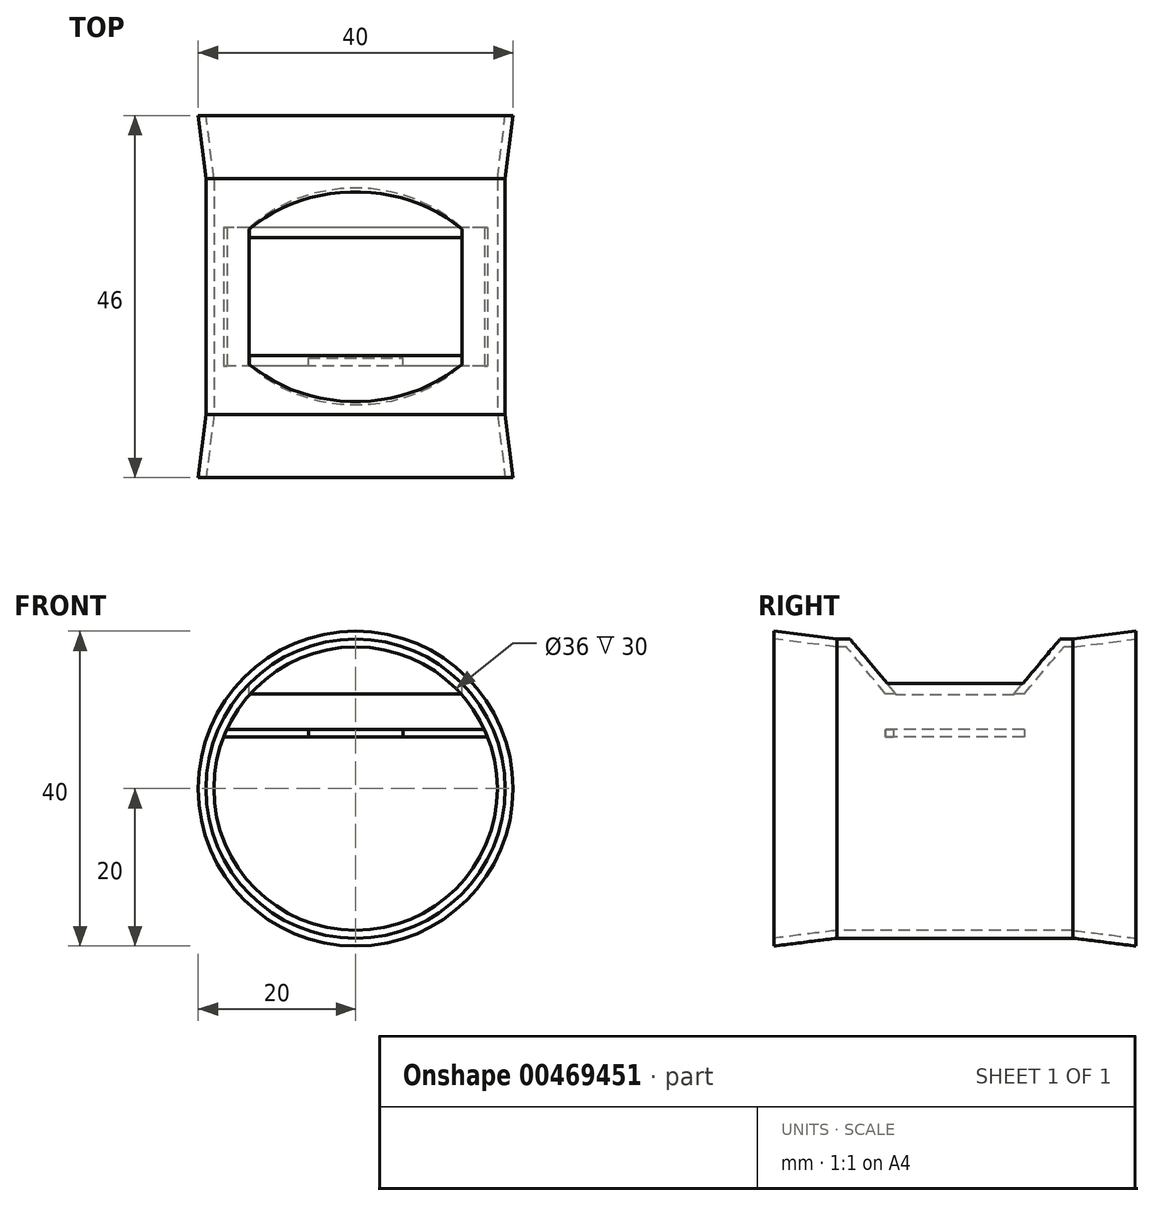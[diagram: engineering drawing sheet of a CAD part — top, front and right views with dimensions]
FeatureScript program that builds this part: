
annotation { "Feature Type Name" : "Feature", "Feature Type Description" : "" }
export const myFeature = defineFeature(function(context is Context, id is Id, definition is map)
    precondition{}
    {
        {
            var Q0;
            Q0=qCreatedBy(makeId("Right.planeOp"),FACE);
            var sketch = newSketch(context, id + "F0", { "sketchPlane" : qUnion([Q0])});
            skLineSegment(sketch, "E0", {"start": v(-23, 19) * mm, "end": v(-15, 18) * mm});
            skLineSegment(sketch, "E1", {"start": v(-15, 18) * mm, "end": v(0, 18) * mm});
            skLineSegment(sketch, "E2.0", {"start": v(-15, 19) * mm, "end": v(0, 19) * mm});
            skLineSegment(sketch, "E3", {"start": v(-15, 19) * mm, "end": v(-23, 20) * mm});
            skLineSegment(sketch, "E4", {"start": v(-23, 20) * mm, "end": v(-23, 19) * mm});
            skLineSegment(sketch, "E5.MirrorCS", {"start": v(23, 20) * mm, "end": v(23, 19) * mm});
            skLineSegment(sketch, "E6.MirrorCS", {"start": v(15, 19) * mm, "end": v(23, 20) * mm});
            skLineSegment(sketch, "E7.MirrorCS", {"start": v(15, 18) * mm, "end": v(0, 18) * mm});
            skLineSegment(sketch, "E8.MirrorCS", {"start": v(23, 19) * mm, "end": v(15, 18) * mm});
            skLineSegment(sketch, "E9.MirrorCS", {"start": v(15, 19) * mm, "end": v(0, 19) * mm});
            skLineSegment(sketch, "E10", {"start": v(-69.17, 0) * mm, "end": v(69.34, 0) * mm});
            skLineSegment(sketch, "E11", {"start": v(-12.5, 18) * mm, "end": v(-7.5, 12.04) * mm});
            skLineSegment(sketch, "E12", {"start": v(-7.5, 12.04) * mm, "end": v(-8.8, 12.04) * mm});
            skLineSegment(sketch, "E13", {"start": v(-8.8, 12.04) * mm, "end": v(-13.8, 18) * mm});
            skLineSegment(sketch, "E14.MirrorCS", {"start": v(12.5, 18) * mm, "end": v(7.5, 12.04) * mm});
            skLineSegment(sketch, "E15.MirrorCS", {"start": v(8.8, 12.04) * mm, "end": v(13.8, 18) * mm});
            skLineSegment(sketch, "E16.MirrorCS", {"start": v(7.5, 12.04) * mm, "end": v(8.8, 12.04) * mm});
            skLineSegment(sketch, "E17", {"start": v(-7.5, 12.04) * mm, "end": v(7.5, 12.04) * mm});
            skLineSegment(sketch, "E18", {"start": v(12.5, 18) * mm, "end": v(13.34, 19) * mm});
            skLineSegment(sketch, "E19", {"start": v(-12.5, 18) * mm, "end": v(-13.34, 19) * mm});
            skLineSegment(sketch, "E20.bottom", {"start": v(-8.8, 7.54) * mm, "end": v(8.8, 7.54) * mm});
            skLineSegment(sketch, "E20.top", {"start": v(-8.8, 6.54) * mm, "end": v(8.8, 6.54) * mm});
            skLineSegment(sketch, "E20.left", {"start": v(-8.8, 7.54) * mm, "end": v(-8.8, 6.54) * mm});
            skLineSegment(sketch, "E20.right", {"start": v(8.8, 7.54) * mm, "end": v(8.8, 6.54) * mm});
            skLineSegment(sketch, "E21", {"start": v(-7.5, 12.04) * mm, "end": v(-7.5, 11.04) * mm});
            skLineSegment(sketch, "E22", {"start": v(-7.5, 11.04) * mm, "end": v(7.5, 11.04) * mm});
            skLineSegment(sketch, "E23", {"start": v(7.5, 11.04) * mm, "end": v(7.5, 12.04) * mm});
            skLineSegment(sketch, "E24", {"start": v(-7.8, 7.54) * mm, "end": v(-7.8, 6.54) * mm});
            skSolve(sketch);
        }
        {
            var Q0;
            {var subQ5=sQuery(id+"F0.wireOp",EDGE,"E0");Q0=makeQuery(id+"F0.imprint","IMPRINT",FACE,{"disambiguationData":[TD([[makeQuery(id+"F0.imprint","IMPRINT",EDGE,{"derivedFrom":subQ5}),1.0]])]});}
            var Q1;
            {var subQ0=sQuery(id+"F0.wireOp",EDGE,"wl3TgNvH-qM2r-iR0o-pi6W-xrNkjA2WT0vf");var subQ1=sQuery(id+"F0.wireOp",EDGE,"E7.MirrorCS");var subQ2=makeQuery(id+"F0.imprint","INTERSECT",VERTEX,{"derivedFrom":[subQ1,subQ0]});Q1=makeQuery(id+"F0.imprint","IMPRINT",FACE,{"disambiguationData":[TD([[makeQuery(id+"F0.imprint","IMPRINT",EDGE,{"disambiguationData":[TD([[subQ2,-1.0]])],"derivedFrom":subQ1}),-1.0]])]});}
            var Q2;
            {var subQ0=sQuery(id+"F0.wireOp",EDGE,"aRFnVEm7-WrF1-xs9J-EZC0-NmZMYpQ3PLDA");var subQ1=sQuery(id+"F0.wireOp",EDGE,"E1");var subQ2=makeQuery(id+"F0.imprint","INTERSECT",VERTEX,{"derivedFrom":[subQ1,subQ0]});Q2=makeQuery(id+"F0.imprint","IMPRINT",FACE,{"disambiguationData":[TD([[makeQuery(id+"F0.imprint","IMPRINT",EDGE,{"disambiguationData":[TD([[subQ2,-1.0]])],"derivedFrom":subQ1}),1.0]])]});}
            var Q3;
            Q3=makeQuery(id+"F0.imprint","IMPRINT",FACE,{"disambiguationData":[TD([[makeQuery(id+"F0.imprint","IMPRINT",EDGE,{"derivedFrom":sQuery(id+"F0.wireOp",EDGE,"E5.MirrorCS")}),-1.0]])]});
            var Q4;
            {var subQ7=sQuery(id+"F0.wireOp",EDGE,"E7.MirrorCS");var subQ9=sQuery(id+"F0.wireOp",EDGE,"E1");var subQ10=makeQuery(id+"F0.imprint","INTERSECT",VERTEX,{"derivedFrom":[subQ9,subQ7]});Q4=makeQuery(id+"F0.imprint","IMPRINT",FACE,{"disambiguationData":[TD([[makeQuery(id+"F0.imprint","IMPRINT",EDGE,{"disambiguationData":[TD([[subQ10,1.0]])],"derivedFrom":subQ9}),1.0]])]});}
            var Q5;
            Q5=sQuery(id+"F0.wireOp",EDGE,"E10");
            revolve(context, id + "F1", {"entities" : qUnion([Q0, Q1, Q2, Q3, Q4]), "axis" : qUnion([Q5]), "revolveType" : RevolveType.FULL});
        }
        {
            var Q0;
            {var subQ0=sQuery(id+"F0.wireOp",EDGE,"E14.MirrorCS");Q0=makeQuery(id+"F0.imprint","IMPRINT",FACE,{"disambiguationData":[TD([[makeQuery(id+"F0.imprint","IMPRINT",EDGE,{"derivedFrom":subQ0}),1.0]])]});}
            var Q1;
            {var subQ0=sQuery(id+"F0.wireOp",EDGE,"E11");Q1=makeQuery(id+"F0.imprint","IMPRINT",FACE,{"disambiguationData":[TD([[makeQuery(id+"F0.imprint","IMPRINT",EDGE,{"derivedFrom":subQ0}),-1.0]])]});}
            var Q2;
            Q2=makeQuery(id+"F1.opRevolve","SWEPT_FACE",FACE,{"disambiguationData":[OSD([sQuery(id+"F0.wireOp",EDGE,"E1"),sQuery(id+"F0.wireOp",EDGE,"E7.MirrorCS")])]});
            var Q3;
            Q3=makeQuery(id+"F1.opRevolve","SWEPT_FACE",FACE,{"disambiguationData":[OSD([sQuery(id+"F0.wireOp",EDGE,"E1"),sQuery(id+"F0.wireOp",EDGE,"E7.MirrorCS")])]});
            extrude(context, id + "F2", {"entities" : qUnion([Q0, Q1]), "operationType" : NewBodyOperationType.ADD, "endBound" : BoundingType.UP_TO_SURFACE, "depth" : 25 * mm, "endBoundEntityFace" : qUnion([Q2]), "offsetDistance" : 25 * mm, "hasSecondDirection" : true, "secondDirectionBound" : SecondDirectionBoundingType.UP_TO_SURFACE, "secondDirectionOppositeDirection" : true, "secondDirectionDepth" : 25 * mm, "secondDirectionBoundEntityFace" : qUnion([Q3])});
        }
        {
            var Q0;
            {var subQ3=sQuery(id+"F0.wireOp",EDGE,"E18");Q0=makeQuery(id+"F0.imprint","IMPRINT",FACE,{"disambiguationData":[TD([[makeQuery(id+"F0.imprint","IMPRINT",EDGE,{"derivedFrom":subQ3}),1.0]])]});}
            var Q1;
            {var subQ1=sQuery(id+"F0.wireOp",EDGE,"E11");Q1=makeQuery(id+"F0.imprint","IMPRINT",FACE,{"disambiguationData":[TD([[makeQuery(id+"F0.imprint","IMPRINT",EDGE,{"derivedFrom":subQ1}),1.0]])]});}
            var Q2;
            Q2=makeQuery(id+"F0.imprint","IMPRINT",FACE,{"disambiguationData":[TD([[makeQuery(id+"F0.imprint","IMPRINT",EDGE,{"derivedFrom":sQuery(id+"F0.wireOp",EDGE,"E17")}),-1.0]])]});
            extrude(context, id + "F3", {"entities" : qUnion([Q0, Q1, Q2]), "operationType" : NewBodyOperationType.REMOVE, "depth" : 13.5 * mm, "offsetDistance" : 25 * mm, "hasSecondDirection" : true, "secondDirectionOppositeDirection" : true, "secondDirectionDepth" : 13.5 * mm});
        }
        {
            var Q0;
            Q0=makeQuery(id+"F0.imprint","IMPRINT",FACE,{"disambiguationData":[TD([[makeQuery(id+"F0.imprint","IMPRINT",EDGE,{"derivedFrom":sQuery(id+"F0.wireOp",EDGE,"E20.bottom")}),-1.0]])]});
            var Q1;
            Q1=makeQuery(id+"F1.opRevolve","SWEPT_FACE",FACE,{"disambiguationData":[OSD([sQuery(id+"F0.wireOp",EDGE,"E1"),sQuery(id+"F0.wireOp",EDGE,"E7.MirrorCS")])]});
            var Q2;
            Q2=makeQuery(id+"F1.opRevolve","SWEPT_FACE",FACE,{"disambiguationData":[OSD([sQuery(id+"F0.wireOp",EDGE,"E1"),sQuery(id+"F0.wireOp",EDGE,"E7.MirrorCS")])]});
            extrude(context, id + "F4", {"entities" : qUnion([Q0]), "operationType" : NewBodyOperationType.ADD, "endBound" : BoundingType.UP_TO_SURFACE, "depth" : 25 * mm, "endBoundEntityFace" : qUnion([Q1]), "offsetDistance" : 25 * mm, "hasSecondDirection" : true, "secondDirectionBound" : SecondDirectionBoundingType.UP_TO_SURFACE, "secondDirectionOppositeDirection" : true, "secondDirectionDepth" : 25 * mm, "secondDirectionBoundEntityFace" : qUnion([Q2])});
        }
        {
            var Q0;
            {var subQ0=sQuery(id+"F0.wireOp",EDGE,"E20.left");Q0=makeQuery(id+"F0.imprint","IMPRINT",FACE,{"disambiguationData":[TD([[makeQuery(id+"F0.imprint","IMPRINT",EDGE,{"derivedFrom":subQ0}),1.0]])]});}
            extrude(context, id + "F5", {"entities" : qUnion([Q0]), "operationType" : NewBodyOperationType.REMOVE, "oppositeDirection" : true, "depth" : 6 * mm, "offsetDistance" : 25 * mm, "hasSecondDirection" : true, "secondDirectionOppositeDirection" : false, "secondDirectionDepth" : 6 * mm});
        }
    });
